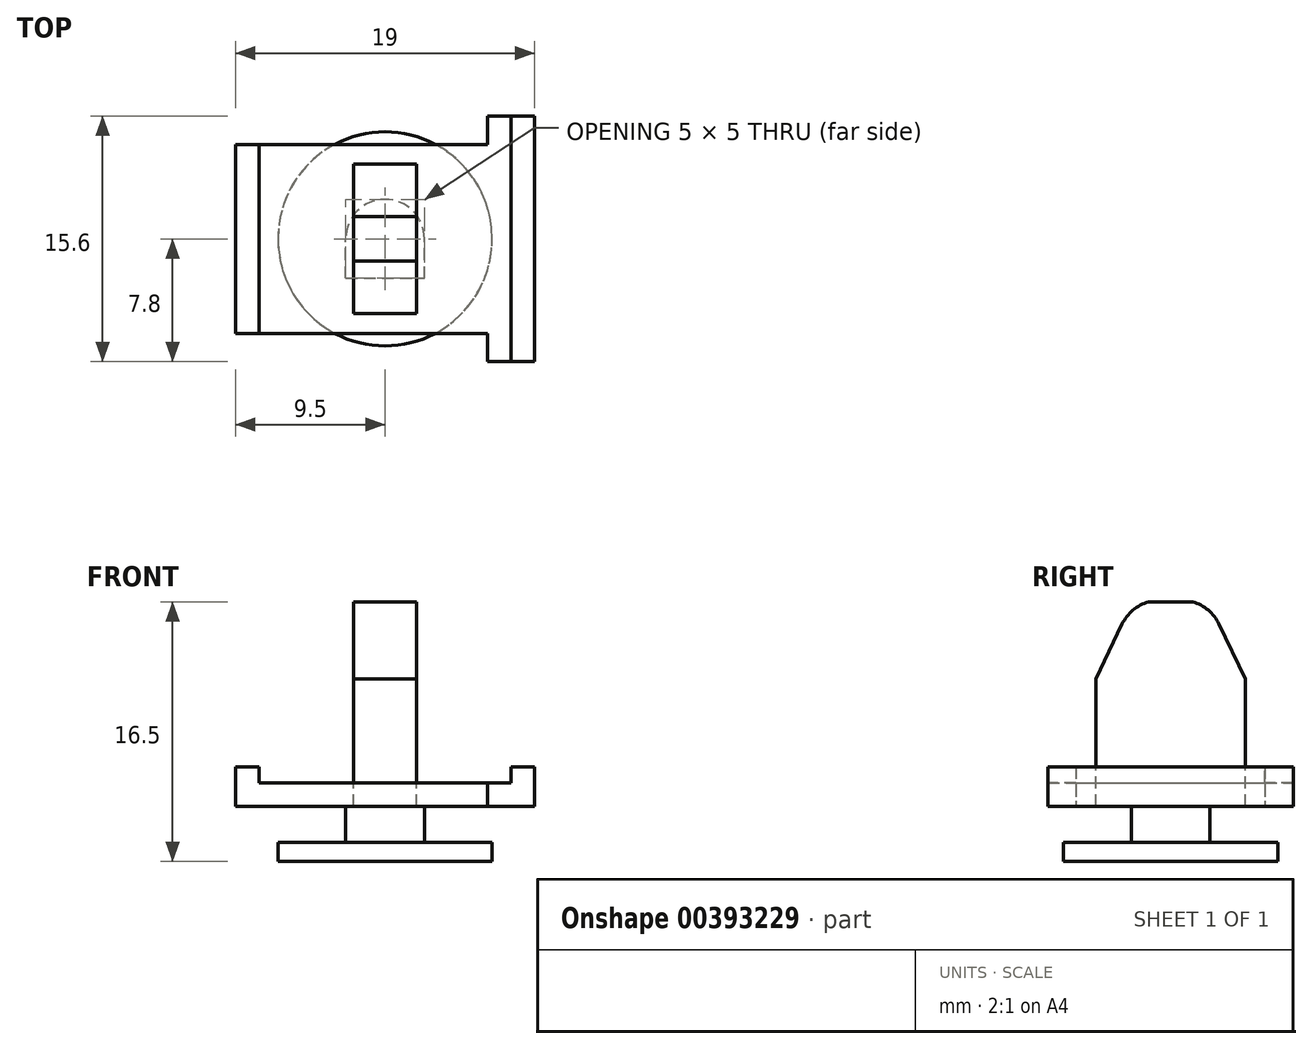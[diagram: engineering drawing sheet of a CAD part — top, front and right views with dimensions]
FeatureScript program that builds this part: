
annotation { "Feature Type Name" : "Feature", "Feature Type Description" : "" }
export const myFeature = defineFeature(function(context is Context, id is Id, definition is map)
    precondition{}
    {
        {
            var Q0;
            Q0=qCreatedBy(makeId("Top.planeOp"),FACE);
            var sketch = newSketch(context, id + "F0", { "sketchPlane" : qUnion([Q0])});
            skLineSegment(sketch, "E0.bottom", {"start": v(9.5, -7.8) * mm, "end": v(6.5, -7.8) * mm});
            skLineSegment(sketch, "E0.top", {"start": v(9.5, 7.8) * mm, "end": v(6.5, 7.8) * mm});
            skLineSegment(sketch, "E0.left", {"start": v(9.5, -7.8) * mm, "end": v(9.5, 7.8) * mm});
            skLineSegment(sketch, "E0.right", {"start": v(-9.5, -6) * mm, "end": v(-9.5, 6) * mm});
            skPoint(sketch, "E0.middle", {"position": v(0, 0) * mm});
            skLineSegment(sketch, "E1", {"start": v(6.5, 7.8) * mm, "end": v(6.5, 6) * mm});
            skLineSegment(sketch, "E2", {"start": v(6.5, 6) * mm, "end": v(-9.5, 6) * mm});
            skLineSegment(sketch, "E3", {"start": v(-9.5, -6) * mm, "end": v(6.5, -6) * mm});
            skLineSegment(sketch, "E4", {"start": v(6.5, -6) * mm, "end": v(6.5, -7.8) * mm});
            skSolve(sketch);
        }
        {
            var Q0;
            Q0=makeQuery(id+"F0.imprint","IMPRINT",FACE,{"disambiguationData":[TD([[makeQuery(id+"F0.imprint","IMPRINT",EDGE,{"derivedFrom":sQuery(id+"F0.wireOp",EDGE,"E0.bottom")}),-1.0]])]});
            extrude(context, id + "F1", {"entities" : qUnion([Q0]), "depth" : 2.5 * mm, "offsetDistance" : 25 * mm});
        }
        {
            var Q0;
            Q0=makeQuery(id+"F1.opExtrude","CAP_FACE",FACE,{"disambiguationData":[OSD([sQuery(id+"F0.wireOp",EDGE,"E0.bottom"),sQuery(id+"F0.wireOp",EDGE,"E0.top"),sQuery(id+"F0.wireOp",EDGE,"E0.left"),sQuery(id+"F0.wireOp",EDGE,"E0.right"),sQuery(id+"F0.wireOp",EDGE,"E1"),sQuery(id+"F0.wireOp",EDGE,"E2"),sQuery(id+"F0.wireOp",EDGE,"E3"),sQuery(id+"F0.wireOp",EDGE,"E4")])],"isStart":false});
            var sketch = newSketch(context, id + "F2", { "sketchPlane" : qUnion([Q0])});
            skLineSegment(sketch, "E5.bottom", {"start": v(8, -9.64) * mm, "end": v(-8, -9.64) * mm});
            skLineSegment(sketch, "E5.top", {"start": v(8, 9.64) * mm, "end": v(-8, 9.64) * mm});
            skLineSegment(sketch, "E5.left", {"start": v(8, -9.64) * mm, "end": v(8, 9.64) * mm});
            skLineSegment(sketch, "E5.right", {"start": v(-8, -9.64) * mm, "end": v(-8, 9.64) * mm});
            skPoint(sketch, "E5.middle", {"position": v(0, 0) * mm});
            skSolve(sketch);
        }
        {
            var Q0;
            Q0 = qSketchRegion(id + "F2", true);
            extrude(context, id + "F3", {"entities" : qUnion([Q0]), "operationType" : NewBodyOperationType.REMOVE, "oppositeDirection" : true, "depth" : 1 * mm, "offsetDistance" : 25 * mm});
        }
        {
            var Q0;
            Q0=makeQuery(id+"F1.opExtrude","CAP_FACE",FACE,{"disambiguationData":[OSD([sQuery(id+"F0.wireOp",EDGE,"E0.bottom"),sQuery(id+"F0.wireOp",EDGE,"E0.top"),sQuery(id+"F0.wireOp",EDGE,"E0.left"),sQuery(id+"F0.wireOp",EDGE,"E0.right"),sQuery(id+"F0.wireOp",EDGE,"E1"),sQuery(id+"F0.wireOp",EDGE,"E2"),sQuery(id+"F0.wireOp",EDGE,"E3"),sQuery(id+"F0.wireOp",EDGE,"E4")])],"isStart":true});
            var sketch = newSketch(context, id + "F4", { "sketchPlane" : qUnion([Q0])});
            skArc(sketch, "E6", {"start": v(-2.5, 0) * mm, "mid": v(0, -2.5) * mm, "end": v(2.5, 0) * mm});
            skLineSegment(sketch, "E7", {"start": v(-2.5, 2.5) * mm, "end": v(2.5, 2.5) * mm});
            skLineSegment(sketch, "E8", {"start": v(-2.5, 2.5) * mm, "end": v(-2.5, 0) * mm});
            skLineSegment(sketch, "E9", {"start": v(2.5, 2.5) * mm, "end": v(2.5, 0) * mm});
            skSolve(sketch);
        }
        {
            var Q0;
            Q0 = qSketchRegion(id + "F4", true);
            extrude(context, id + "F5", {"entities" : qUnion([Q0]), "operationType" : NewBodyOperationType.ADD, "depth" : 2.3 * mm, "offsetDistance" : 25 * mm});
        }
        {
            var Q0;
            Q0=makeQuery(id+"F5.opExtrude","CAP_FACE",FACE,{"disambiguationData":[OSD([sQuery(id+"F4.wireOp",EDGE,"E6")])],"isStart":false});
            var sketch = newSketch(context, id + "F6", { "sketchPlane" : qUnion([Q0])});
            skCircle(sketch, "E10", {"center": v(0, 0) * mm, "radius": 6.8 * mm});
            skSolve(sketch);
        }
        {
            var Q0;
            Q0 = qSketchRegion(id + "F6", true);
            extrude(context, id + "F7", {"entities" : qUnion([Q0]), "operationType" : NewBodyOperationType.ADD, "depth" : 1.2 * mm, "offsetDistance" : 25 * mm});
        }
        {
            var Q0;
            Q0=qCreatedBy(makeId("Right.planeOp"),FACE);
            var sketch = newSketch(context, id + "F8", { "sketchPlane" : qUnion([Q0])});
            skLineSegment(sketch, "E11", {"start": v(-4.75, 0) * mm, "end": v(-4.75, 8.1) * mm});
            skLineSegment(sketch, "E12", {"start": v(-4.75, 8.1) * mm, "end": v(-3.08, 11.57) * mm});
            skArc(sketch, "E13", {"start": v(-1.4, 13) * mm, "mid": v(-2.4, 12.46) * mm, "end": v(-3.08, 11.57) * mm});
            skLineSegment(sketch, "E14", {"start": v(-1.4, 13) * mm, "end": v(0, 13) * mm});
            skLineSegment(sketch, "E15", {"start": v(0, 0) * mm, "end": v(0, 17.73) * mm, "construction": true});
            skLineSegment(sketch, "E16.MirrorCS", {"start": v(1.4, 13) * mm, "end": v(0, 13) * mm});
            skArc(sketch, "E17.MirrorCS", {"start": v(1.4, 13) * mm, "mid": v(2.4, 12.46) * mm, "end": v(3.08, 11.57) * mm});
            skLineSegment(sketch, "E18.MirrorCS", {"start": v(4.75, 0) * mm, "end": v(4.75, 8.1) * mm});
            skLineSegment(sketch, "E19.MirrorCS", {"start": v(4.75, 8.1) * mm, "end": v(3.08, 11.57) * mm});
            skLineSegment(sketch, "E20", {"start": v(-4.75, 0) * mm, "end": v(4.75, 0) * mm});
            skSolve(sketch);
        }
        {
            var Q0;
            Q0 = qSketchRegion(id + "F8", true);
            extrude(context, id + "F9", {"entities" : qUnion([Q0]), "depth" : 2 * mm, "offsetDistance" : 25 * mm, "hasSecondDirection" : true, "secondDirectionOppositeDirection" : true, "secondDirectionDepth" : 2 * mm});
        }
    });
